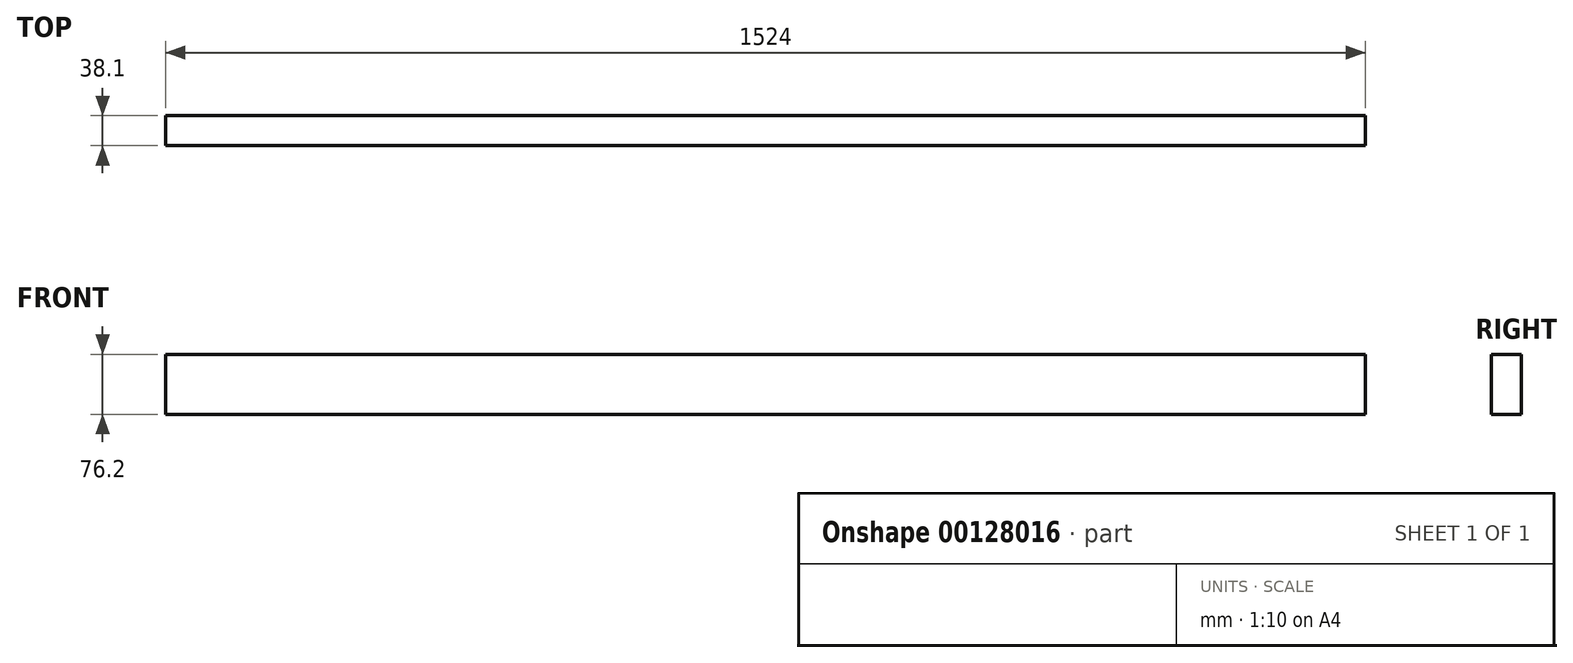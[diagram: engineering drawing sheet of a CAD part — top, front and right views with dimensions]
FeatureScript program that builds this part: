
annotation { "Feature Type Name" : "Feature", "Feature Type Description" : "" }
export const myFeature = defineFeature(function(context is Context, id is Id, definition is map)
    precondition{}
    {
        {
            var Q0;
            Q0=qCreatedBy(makeId("Top.planeOp"),FACE);
            var sketch = newSketch(context, id + "F0", { "sketchPlane" : qUnion([Q0])});
            skLineSegment(sketch, "E0.bottom", {"start": v(0, 0) * mm, "end": v(1524, 0) * mm});
            skLineSegment(sketch, "E0.top", {"start": v(0, 38.1) * mm, "end": v(1524, 38.1) * mm});
            skLineSegment(sketch, "E0.left", {"start": v(0, 0) * mm, "end": v(0, 38.1) * mm});
            skLineSegment(sketch, "E0.right", {"start": v(1524, 0) * mm, "end": v(1524, 38.1) * mm});
            skSolve(sketch);
        }
        {
            var Q0;
            Q0=makeQuery(id+"F0.imprint","IMPRINT",FACE,{"disambiguationData":[TD([[makeQuery(id+"F0.imprint","IMPRINT",EDGE,{"derivedFrom":sQuery(id+"F0.wireOp",EDGE,"E0.bottom")}),1.0]])]});
            extrude(context, id + "F1", {"entities" : qUnion([Q0]), "oppositeDirection" : true, "depth" : 76.2 * mm, "offsetDistance" : 25.4 * mm});
        }
    });
